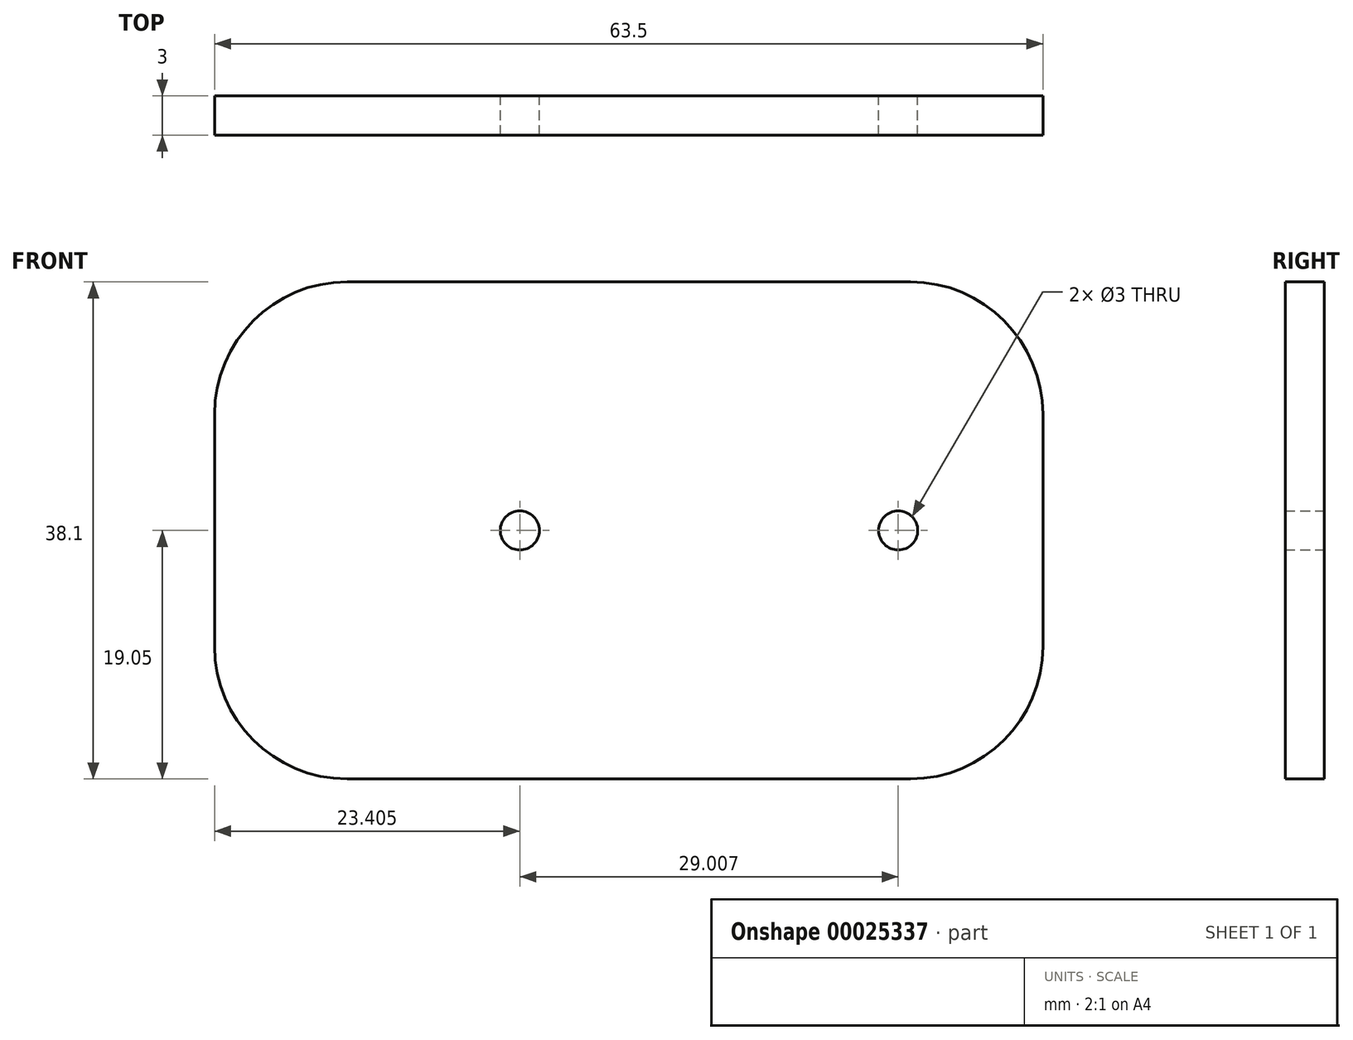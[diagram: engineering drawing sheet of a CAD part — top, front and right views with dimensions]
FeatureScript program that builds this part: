
annotation { "Feature Type Name" : "Feature", "Feature Type Description" : "" }
export const myFeature = defineFeature(function(context is Context, id is Id, definition is map)
    precondition{}
    {
        {
            var Q0;
            Q0=qCreatedBy(makeId("Front.planeOp"),FACE);
            var sketch = newSketch(context, id + "F0", { "sketchPlane" : qUnion([Q0])});
            skLineSegment(sketch, "E0.rect.bottom", {"start": v(31.75, -19.05) * mm, "end": v(-31.75, -19.05) * mm});
            skLineSegment(sketch, "E0.rect.top", {"start": v(31.75, 19.05) * mm, "end": v(-31.75, 19.05) * mm});
            skLineSegment(sketch, "E0.rect.left", {"start": v(31.75, -19.05) * mm, "end": v(31.75, 19.05) * mm});
            skLineSegment(sketch, "E0.rect.right", {"start": v(-31.75, -19.05) * mm, "end": v(-31.75, 19.05) * mm});
            skPoint(sketch, "E0.rect.middle", {"position": v(0, 0) * mm});
            skCircle(sketch, "E1", {"center": v(-8.34, 0) * mm, "radius": 1.5 * mm});
            skCircle(sketch, "E2", {"center": v(20.66, 0) * mm, "radius": 1.5 * mm});
            skLineSegment(sketch, "E3", {"start": v(-8.34, 0) * mm, "end": v(20.66, 0) * mm});
            skSolve(sketch);
        }
        {
            var Q0;
            Q0=makeQuery(id+"F0.imprint","IMPRINT",FACE,{"disambiguationData":[TD([[makeQuery(id+"F0.imprint","IMPRINT",EDGE,{"derivedFrom":sQuery(id+"F0.wireOp",EDGE,"E0.rect.bottom")}),-1.0]])]});
            extrude(context, id + "F1", {"entities" : qUnion([Q0]), "depth" : 3 * mm});
        }
        {
            var Q0;
            Q0=makeQuery(id+"F1.opExtrude","SWEPT_EDGE",EDGE,{"disambiguationData":[OSD([sQuery(id+"F0.wireOp",EDGE,"E0.rect.top"),sQuery(id+"F0.wireOp",EDGE,"E0.rect.left")])]});
            var Q1;
            Q1=makeQuery(id+"F1.opExtrude","SWEPT_EDGE",EDGE,{"disambiguationData":[OSD([sQuery(id+"F0.wireOp",EDGE,"E0.rect.bottom"),sQuery(id+"F0.wireOp",EDGE,"E0.rect.left")])]});
            var Q2;
            Q2=makeQuery(id+"F1.opExtrude","SWEPT_EDGE",EDGE,{"disambiguationData":[OSD([sQuery(id+"F0.wireOp",EDGE,"E0.rect.bottom"),sQuery(id+"F0.wireOp",EDGE,"E0.rect.right")])]});
            var Q3;
            Q3=makeQuery(id+"F1.opExtrude","SWEPT_EDGE",EDGE,{"disambiguationData":[OSD([sQuery(id+"F0.wireOp",EDGE,"E0.rect.top"),sQuery(id+"F0.wireOp",EDGE,"E0.rect.right")])]});
            fillet(context, id + "F2", {"entities" : qUnion([Q0, Q1, Q2, Q3]), "radius" : 10.16 * mm, "tangentPropagation" : true, "allowEdgeOverflow" : false});
        }
    });
